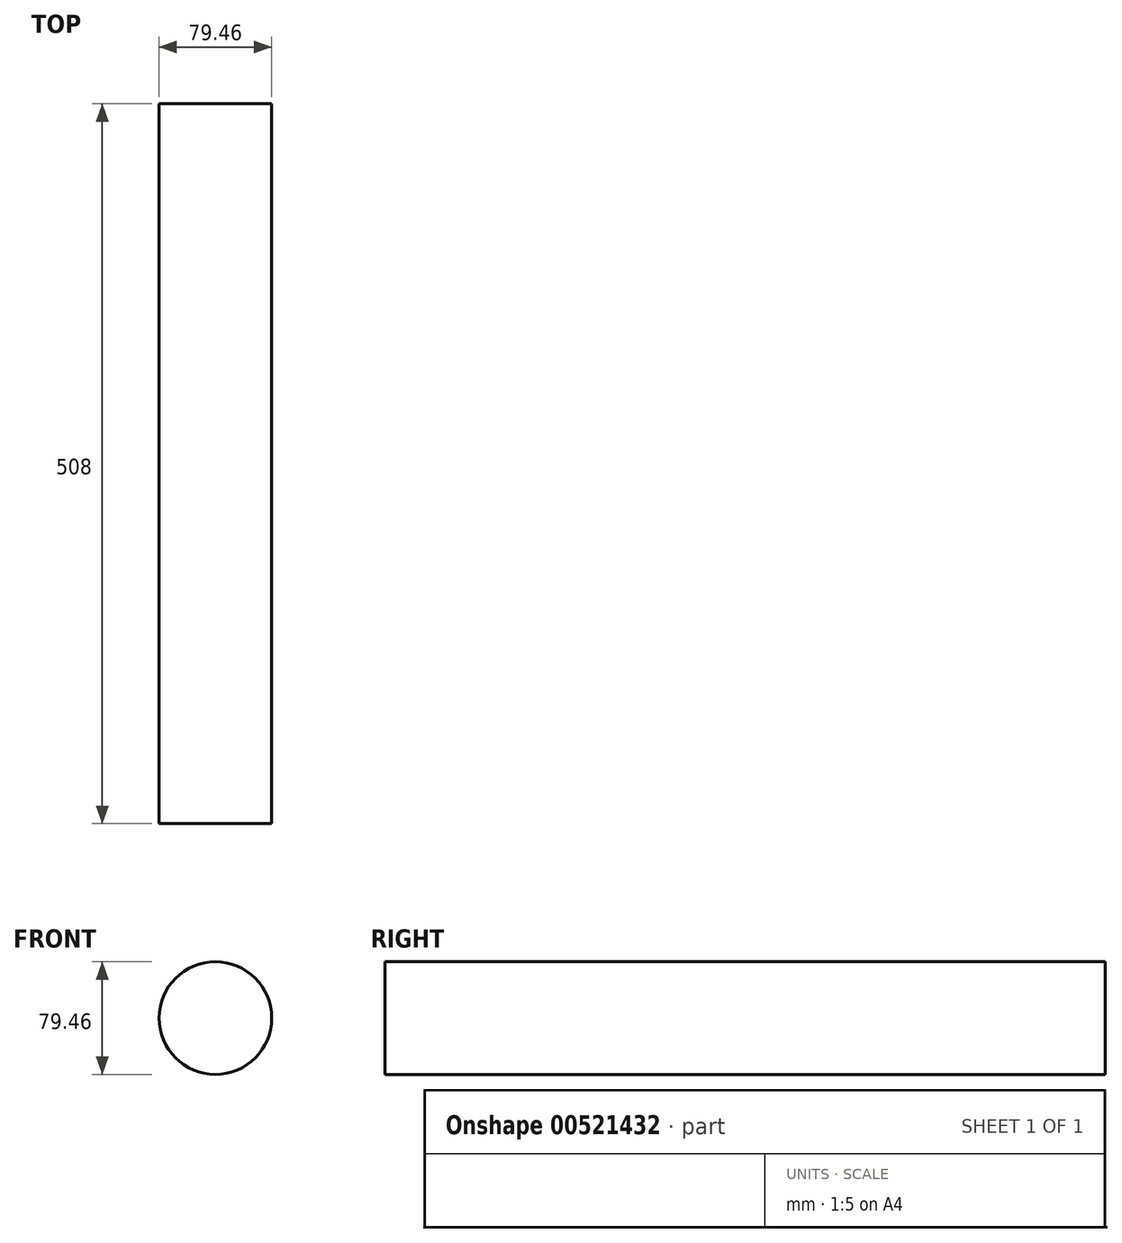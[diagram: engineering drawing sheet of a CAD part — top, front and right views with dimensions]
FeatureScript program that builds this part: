
annotation { "Feature Type Name" : "Feature", "Feature Type Description" : "" }
export const myFeature = defineFeature(function(context is Context, id is Id, definition is map)
    precondition{}
    {
        {
            var Q0;
            Q0=qCreatedBy(makeId("Front.planeOp"),FACE);
            var sketch = newSketch(context, id + "F0", { "sketchPlane" : qUnion([Q0])});
            skCircle(sketch, "E0", {"center": v(0, 0) * mm, "radius": 39.73 * mm});
            skSolve(sketch);
        }
        {
            var Q0;
            Q0=makeQuery(id+"F0.imprint","IMPRINT",FACE,{"disambiguationData":[TD([[makeQuery(id+"F0.imprint","IMPRINT",EDGE,{"derivedFrom":sQuery(id+"F0.wireOp",EDGE,"E0")}),1.0]])]});
            extrude(context, id + "F1", {"entities" : qUnion([Q0]), "depth" : 508 * mm, "offsetDistance" : 25.4 * mm});
        }
    });
